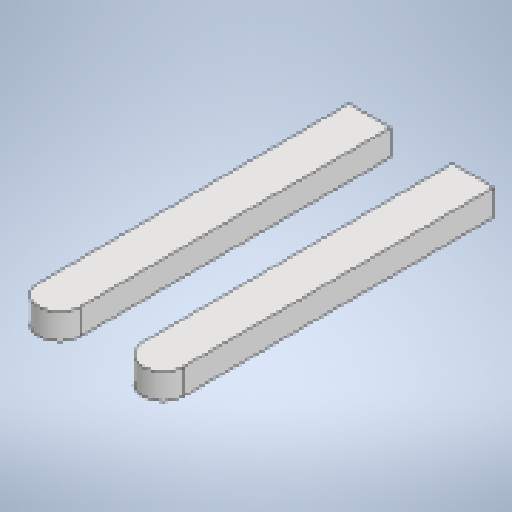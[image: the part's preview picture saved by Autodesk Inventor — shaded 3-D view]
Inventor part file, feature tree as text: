
AUTODESK INVENTOR PART (.ipt)
format: ipt  version: 2025.3 (Build 293356030, 356C)  size: 182,272 bytes
history: native  units: mm
features: extrude x3, sketch x3, projected_geometry x3
ambient origin geometry x8: Origin, YZ Plane, XZ Plane, XY Plane, X Axis, Y Axis, Z Axis, Center Point
bodies: Solid1 (feature_tree)
feature tree (9):
  extrude  "Extrusion1"  Depth=560.0mm
  extrude  "Extrusion2"  Depth=100.0mm TaperAngle=0.0deg
  extrude  "Extrusion3"  Depth=560.0mm
  sketch  "Sketch1"  dims[d0=160.0mm d1=560.0mm]
  sketch  "Sketch2"  dims[d2=1200.0mm d3=100.0mm d4=0.0mm]
  projected_geometry  "Projected Loop1"
  projected_geometry  "Projected Loop2"
  sketch  "Sketch3"  dims[d5=80.0mm d6=560.0mm d7=560.0mm d8=400.0mm d9=500.0mm d10=40.0mm d11=0.0mm d12=40.0mm d13=60.0mm d14=0.0mm]
  projected_geometry  "Projected Loop3"
